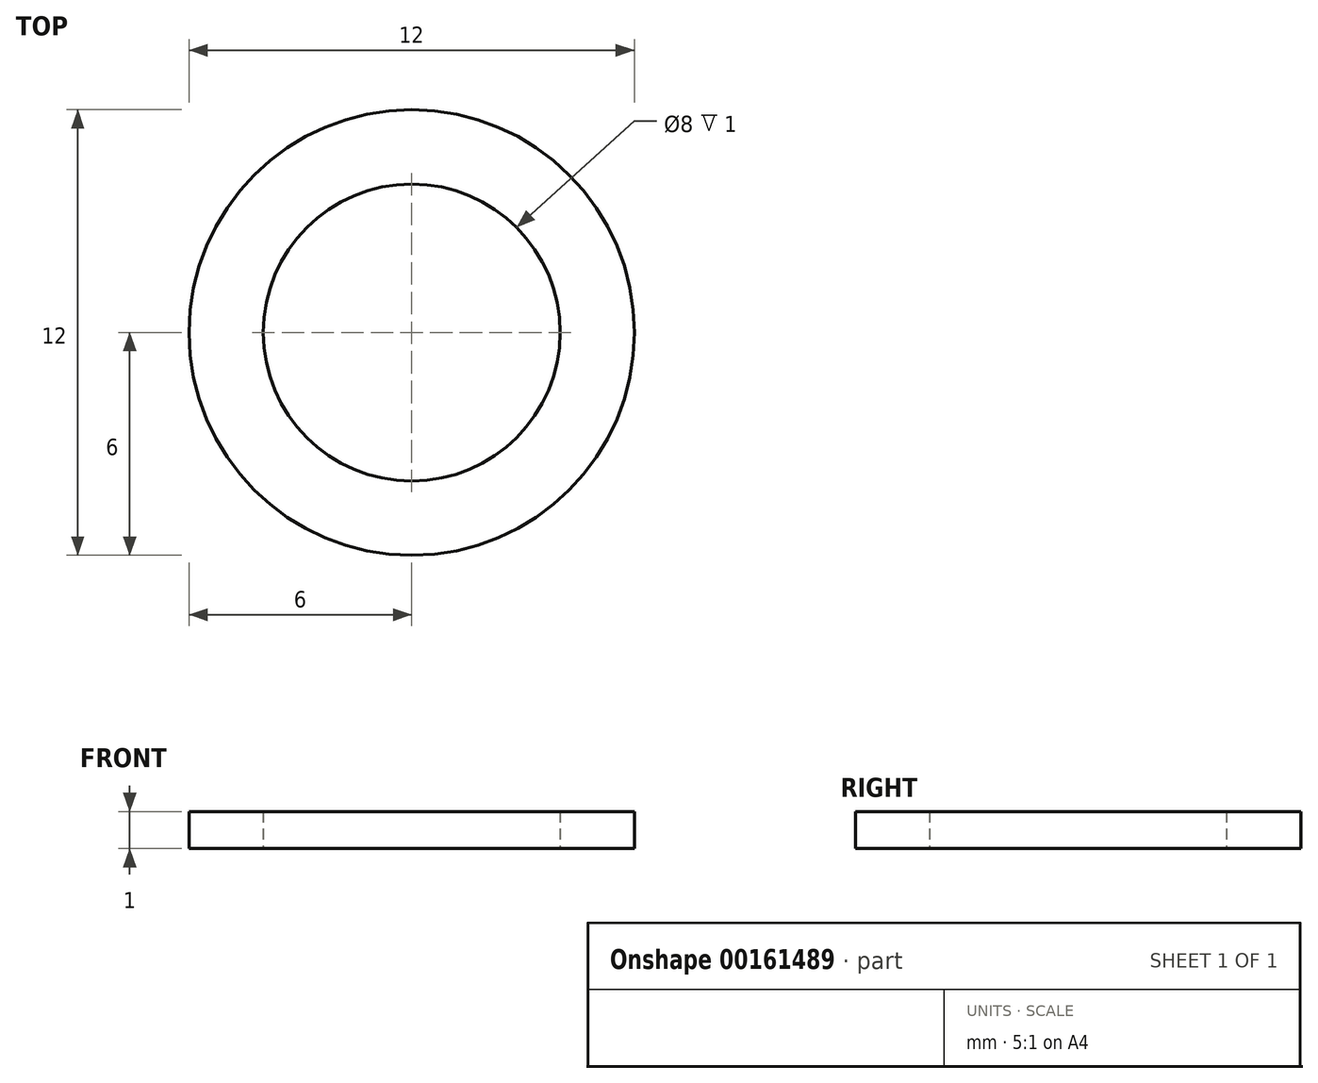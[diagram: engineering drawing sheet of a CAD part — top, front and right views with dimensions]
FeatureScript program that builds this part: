
annotation { "Feature Type Name" : "Feature", "Feature Type Description" : "" }
export const myFeature = defineFeature(function(context is Context, id is Id, definition is map)
    precondition{}
    {
        {
            var Q0;
            Q0=qCreatedBy(makeId("Top.planeOp"),FACE);
            var sketch = newSketch(context, id + "F0", { "sketchPlane" : qUnion([Q0])});
            skCircle(sketch, "E0", {"center": v(0, 0) * mm, "radius": 4 * mm});
            skCircle(sketch, "E1", {"center": v(0, 0) * mm, "radius": 6 * mm});
            skSolve(sketch);
        }
        {
            var Q0;
            Q0 = qSketchRegion(id + "F0", true);
            extrude(context, id + "F1", {"entities" : qUnion([Q0]), "depth" : 1 * mm});
        }
    });
